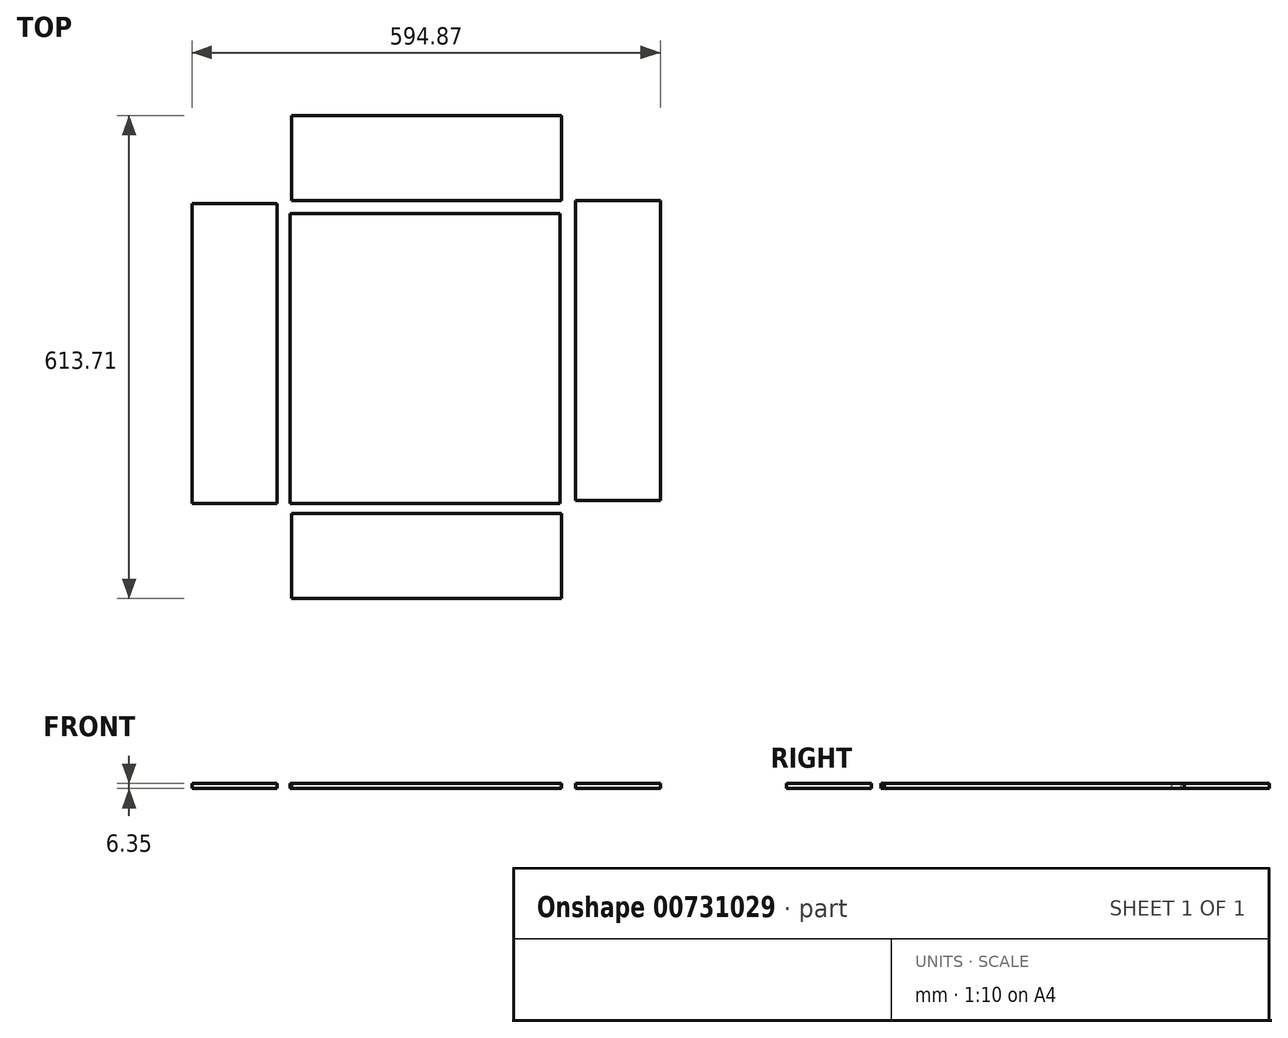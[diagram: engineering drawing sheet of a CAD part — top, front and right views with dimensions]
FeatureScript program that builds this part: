
annotation { "Feature Type Name" : "Feature", "Feature Type Description" : "" }
export const myFeature = defineFeature(function(context is Context, id is Id, definition is map)
    precondition{}
    {
        {
            var Q0;
            Q0=qCreatedBy(makeId("Top.planeOp"),FACE);
            var sketch = newSketch(context, id + "F0", { "sketchPlane" : qUnion([Q0])});
            skLineSegment(sketch, "E0.bottom", {"start": v(-158.9, 225.25) * mm, "end": v(184, 225.25) * mm});
            skLineSegment(sketch, "E0.top", {"start": v(-158.9, -143.05) * mm, "end": v(184, -143.05) * mm});
            skLineSegment(sketch, "E0.left", {"start": v(-158.9, 225.25) * mm, "end": v(-158.9, -143.05) * mm});
            skLineSegment(sketch, "E0.right", {"start": v(184, 225.25) * mm, "end": v(184, -143.05) * mm});
            skLineSegment(sketch, "E1.bottom", {"start": v(185.5, -155.84) * mm, "end": v(-157.4, -155.84) * mm});
            skLineSegment(sketch, "E1.top", {"start": v(185.5, -263.79) * mm, "end": v(-157.4, -263.79) * mm});
            skLineSegment(sketch, "E1.left", {"start": v(185.5, -155.84) * mm, "end": v(185.5, -263.79) * mm});
            skLineSegment(sketch, "E1.right", {"start": v(-157.4, -155.84) * mm, "end": v(-157.4, -263.79) * mm});
            skLineSegment(sketch, "E2.bottom", {"start": v(185.5, 349.92) * mm, "end": v(-157.4, 349.92) * mm});
            skLineSegment(sketch, "E2.top", {"start": v(185.5, 241.97) * mm, "end": v(-157.4, 241.97) * mm});
            skLineSegment(sketch, "E2.left", {"start": v(185.5, 349.92) * mm, "end": v(185.5, 241.97) * mm});
            skLineSegment(sketch, "E2.right", {"start": v(-157.4, 349.92) * mm, "end": v(-157.4, 241.97) * mm});
            skLineSegment(sketch, "E3.bottom", {"start": v(311.27, 241.97) * mm, "end": v(203.32, 241.97) * mm});
            skLineSegment(sketch, "E3.top", {"start": v(311.27, -139.03) * mm, "end": v(203.32, -139.03) * mm});
            skLineSegment(sketch, "E3.left", {"start": v(311.27, 241.97) * mm, "end": v(311.27, -139.03) * mm});
            skLineSegment(sketch, "E3.right", {"start": v(203.32, 241.97) * mm, "end": v(203.32, -139.03) * mm});
            skLineSegment(sketch, "E4.bottom", {"start": v(-175.65, 237.76) * mm, "end": v(-283.6, 237.76) * mm});
            skLineSegment(sketch, "E4.top", {"start": v(-175.65, -143.24) * mm, "end": v(-283.6, -143.24) * mm});
            skLineSegment(sketch, "E4.left", {"start": v(-175.65, 237.76) * mm, "end": v(-175.65, -143.24) * mm});
            skLineSegment(sketch, "E4.right", {"start": v(-283.6, 237.76) * mm, "end": v(-283.6, -143.24) * mm});
            skSolve(sketch);
        }
        {
            var Q0;
            Q0=makeQuery(id+"F0.imprint","IMPRINT",FACE,{"disambiguationData":[TD([[makeQuery(id+"F0.imprint","IMPRINT",EDGE,{"derivedFrom":sQuery(id+"F0.wireOp",EDGE,"E0.bottom")}),-1.0]])]});
            extrude(context, id + "F1", {"entities" : qUnion([Q0]), "depth" : 6.35 * mm, "offsetDistance" : 25.4 * mm});
        }
        {
            var Q0;
            Q0=makeQuery(id+"F0.imprint","IMPRINT",FACE,{"disambiguationData":[TD([[makeQuery(id+"F0.imprint","IMPRINT",EDGE,{"derivedFrom":sQuery(id+"F0.wireOp",EDGE,"E3.bottom")}),1.0]])]});
            var Q1;
            Q1=makeQuery(id+"F0.imprint","IMPRINT",FACE,{"disambiguationData":[TD([[makeQuery(id+"F0.imprint","IMPRINT",EDGE,{"derivedFrom":sQuery(id+"F0.wireOp",EDGE,"E1.bottom")}),1.0]])]});
            var Q2;
            Q2=makeQuery(id+"F0.imprint","IMPRINT",FACE,{"disambiguationData":[TD([[makeQuery(id+"F0.imprint","IMPRINT",EDGE,{"derivedFrom":sQuery(id+"F0.wireOp",EDGE,"E4.bottom")}),1.0]])]});
            var Q3;
            Q3=makeQuery(id+"F0.imprint","IMPRINT",FACE,{"disambiguationData":[TD([[makeQuery(id+"F0.imprint","IMPRINT",EDGE,{"derivedFrom":sQuery(id+"F0.wireOp",EDGE,"E2.bottom")}),1.0]])]});
            extrude(context, id + "F2", {"entities" : qUnion([Q0, Q1, Q2, Q3]), "depth" : 6.35 * mm, "offsetDistance" : 25.4 * mm});
        }
    });
